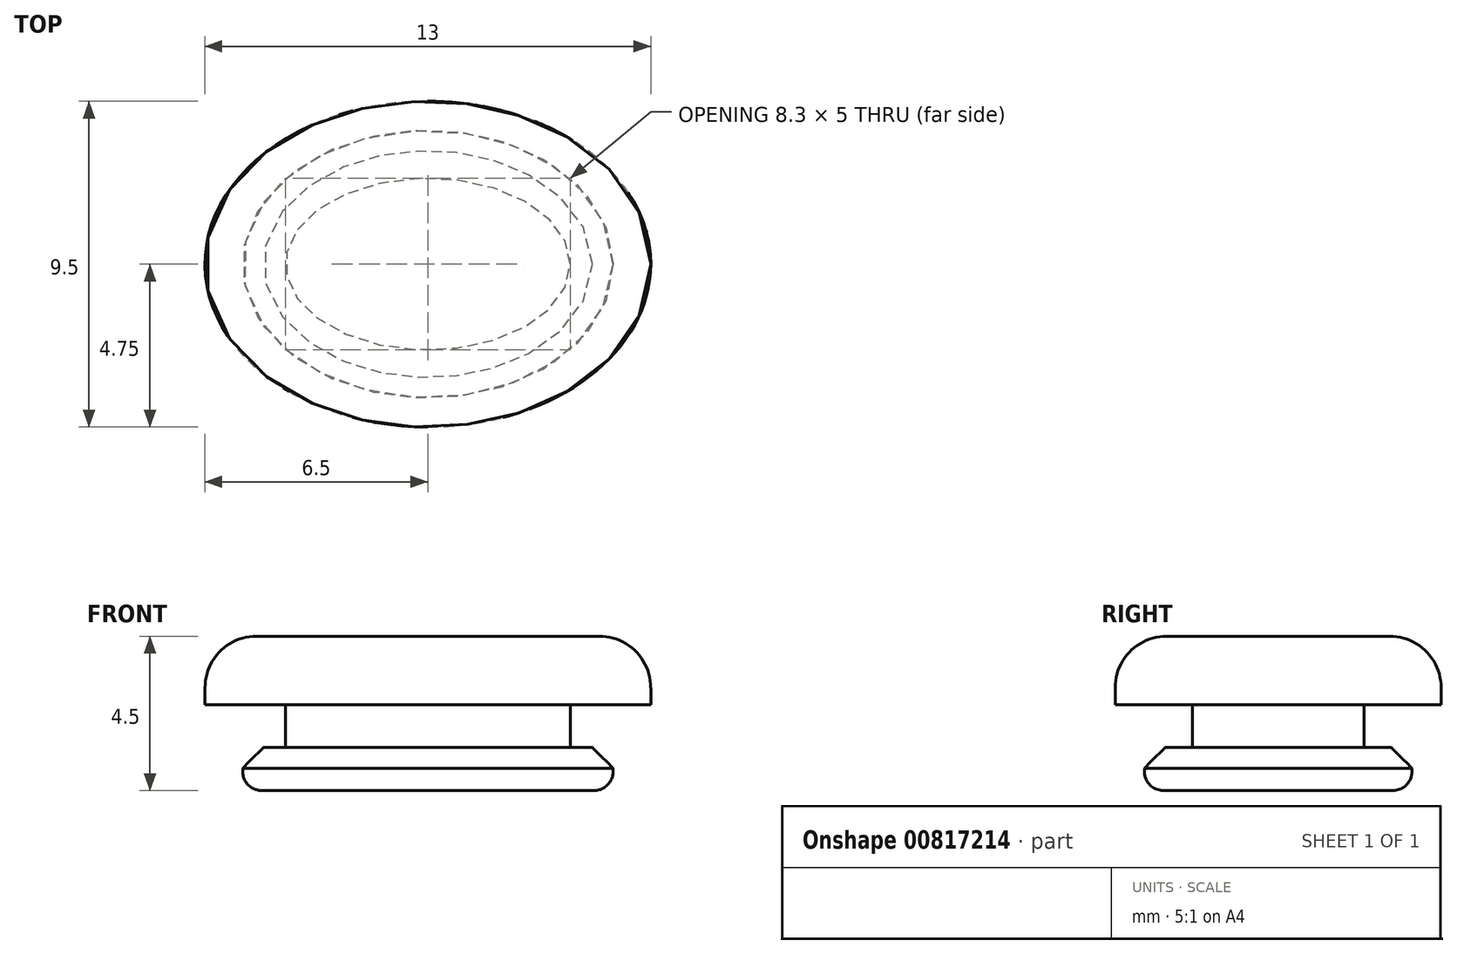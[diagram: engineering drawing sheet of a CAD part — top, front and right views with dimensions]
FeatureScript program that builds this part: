
annotation { "Feature Type Name" : "Feature", "Feature Type Description" : "" }
export const myFeature = defineFeature(function(context is Context, id is Id, definition is map)
    precondition{}
    {
        {
            var Q0;
            Q0=qCreatedBy(makeId("Top.planeOp"),FACE);
            var sketch = newSketch(context, id + "F0", { "sketchPlane" : qUnion([Q0])});
            skEllipse(sketch, "E0", {"center": v(0, 0) * mm, "majorRadius": 6.5 * mm, "minorRadius": 4.75 * mm, "majorAxis": v(1, 0)});
            skEllipse(sketch, "E1", {"center": v(0, 0) * mm, "majorRadius": 5.4 * mm, "minorRadius": 3.9 * mm, "majorAxis": v(1, 0)});
            skEllipse(sketch, "E2", {"center": v(0, 0) * mm, "majorRadius": 4.15 * mm, "minorRadius": 2.5 * mm, "majorAxis": v(1, 0)});
            skSolve(sketch);
        }
        {
            var Q0;
            Q0=makeQuery(id+"F0.imprint","IMPRINT",FACE,{"disambiguationData":[TD([[makeQuery(id+"F0.imprint","IMPRINT",EDGE,{"derivedFrom":sQuery(id+"F0.wireOp",EDGE,"E0")}),1.0]])]});
            var Q1;
            Q1=makeQuery(id+"F0.imprint","IMPRINT",FACE,{"disambiguationData":[TD([[makeQuery(id+"F0.imprint","IMPRINT",EDGE,{"derivedFrom":sQuery(id+"F0.wireOp",EDGE,"E1")}),1.0]])]});
            var Q2;
            Q2=makeQuery(id+"F0.imprint","IMPRINT",FACE,{"disambiguationData":[TD([[makeQuery(id+"F0.imprint","IMPRINT",EDGE,{"derivedFrom":sQuery(id+"F0.wireOp",EDGE,"E2")}),1.0]])]});
            extrude(context, id + "F1", {"entities" : qUnion([Q0, Q1, Q2]), "depth" : 2 * mm, "offsetDistance" : 25 * mm});
        }
        {
            var Q0;
            Q0=makeQuery(id+"F0.imprint","IMPRINT",FACE,{"disambiguationData":[TD([[makeQuery(id+"F0.imprint","IMPRINT",EDGE,{"derivedFrom":sQuery(id+"F0.wireOp",EDGE,"E2")}),1.0]])]});
            extrude(context, id + "F2", {"entities" : qUnion([Q0]), "operationType" : NewBodyOperationType.ADD, "oppositeDirection" : true, "depth" : 2.5 * mm, "offsetDistance" : 25 * mm});
        }
        {
            var Q0;
            Q0=makeQuery(id+"F0.imprint","IMPRINT",FACE,{"disambiguationData":[TD([[makeQuery(id+"F0.imprint","IMPRINT",EDGE,{"derivedFrom":sQuery(id+"F0.wireOp",EDGE,"E1")}),1.0]])]});
            extrude(context, id + "F3", {"entities" : qUnion([Q0]), "operationType" : NewBodyOperationType.ADD, "oppositeDirection" : true, "depth" : 2.5 * mm, "offsetDistance" : 25 * mm, "hasSecondDirection" : true, "secondDirectionOppositeDirection" : true, "secondDirectionDepth" : 1.25 * mm});
        }
        {
            var Q0;
            Q0=makeQuery(id+"F1.opExtrude","CAP_EDGE",EDGE,{"disambiguationData":[OSD([sQuery(id+"F0.wireOp",EDGE,"E0")])],"isStart":false});
            fillet(context, id + "F4", {"entities" : qUnion([Q0]), "radius" : 1.5 * mm, "tangentPropagation" : true, "allowEdgeOverflow" : false});
        }
        {
            var Q0;
            Q0=makeQuery(id+"F3.opExtrude","CAP_EDGE",EDGE,{"disambiguationData":[OSD([sQuery(id+"F0.wireOp",EDGE,"E1")])],"isStart":false});
            fillet(context, id + "F5", {"entities" : qUnion([Q0]), "radius" : .55 * mm, "tangentPropagation" : true, "allowEdgeOverflow" : false});
        }
        {
            var Q0;
            Q0=makeQuery(id+"F3.opExtrude","CAP_EDGE",EDGE,{"disambiguationData":[OSD([sQuery(id+"F0.wireOp",EDGE,"E2")])],"isStart":true});
            var Q1;
            Q1=makeQuery(id+"F3.opExtrude","CAP_EDGE",EDGE,{"disambiguationData":[OSD([sQuery(id+"F0.wireOp",EDGE,"E1")])],"isStart":true});
            chamfer(context, id + "F6", {"entities" : qUnion([Q0, Q1]), "width" : 0.6 * mm, "tangentPropagation" : true});
        }
    });
